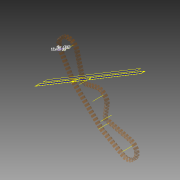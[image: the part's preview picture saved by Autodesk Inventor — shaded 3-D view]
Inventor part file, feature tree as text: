
AUTODESK INVENTOR PART (.ipt)
format: ipt  version: 2014 SP1 (Build 180222100, 222)  size: 551,936 bytes
history: native  units: mm (DEFAULTED — no unit token found)
features: other x93, extrude x84, sketch x4, plane x3, pattern_linear x1
ambient origin geometry x8: Origin, YZ Plane, XZ Plane, XY Plane, X Axis, Y Axis, Z Axis, Center Point
bodies: Body1 (feature_tree), Body2 (feature_tree), Body3 (feature_tree), Body4 (feature_tree), Body5 (feature_tree), Body6 (feature_tree), Body7 (feature_tree), Body8 (feature_tree), Body9 (feature_tree), Body10 (feature_tree), Body11 (feature_tree), Body12 (feature_tree), Body13 (feature_tree), Body14 (feature_tree), Body15 (feature_tree), Body16 (feature_tree), Body17 (feature_tree), Body18 (feature_tree), Body19 (feature_tree), Body20 (feature_tree), Body21 (feature_tree), Body22 (feature_tree), Body23 (feature_tree), Body24 (feature_tree), Body25 (feature_tree), Body26 (feature_tree), Body27 (feature_tree), Body28 (feature_tree), Body29 (feature_tree), Body30 (feature_tree), Body31 (feature_tree), Body32 (feature_tree), Body33 (feature_tree), Body34 (feature_tree), Body35 (feature_tree), Body36 (feature_tree), Body37 (feature_tree), Body38 (feature_tree), Body39 (feature_tree), Body40 (feature_tree), Body41 (feature_tree), Body42 (feature_tree), Body43 (feature_tree), Body44 (feature_tree), Body45 (feature_tree), Body46 (feature_tree), Body47 (feature_tree), Body48 (feature_tree), Body49 (feature_tree), Body50 (feature_tree), Body51 (feature_tree), Body52 (feature_tree), Body53 (feature_tree), Body54 (feature_tree), Body55 (feature_tree), Body56 (feature_tree), Body57 (feature_tree), Body58 (feature_tree), Body59 (feature_tree), Body60 (feature_tree), Body61 (feature_tree), Body62 (feature_tree), Body63 (feature_tree), Body64 (feature_tree), Body65 (feature_tree), Body66 (feature_tree), Body67 (feature_tree), Body68 (feature_tree), Body69 (feature_tree), Body70 (feature_tree), Body71 (feature_tree), Body72 (feature_tree), Body73 (feature_tree), Body74 (feature_tree), Body75 (feature_tree), Body76 (feature_tree), Body77 (feature_tree), Body78 (feature_tree), Body79 (feature_tree), Body80 (feature_tree), Body81 (feature_tree), Body82 (feature_tree), Body83 (feature_tree), Body84 (feature_tree)
feature tree (185):
  sketch  "Sketch Path"  dims[d3=2.682204mm d5=6.981317mm d7=0.0mm d8=0.0mm d9=0.0mm d10=0.0mm d11=0.0mm d12=0.0mm d13=0.0mm d14=0.0mm d15=12.7mm d16=0.0mm d23=6.35mm d24=0.0mm d25=830.0mm]
  other  "Cross Section Plane"
  other  "Work Axis1"
  other  "Work Axis2"
  other  "Work Axis3"
  other  "Work Axis4"
  other  "Work Axis5"
  other  "Work Axis6"
  other  "Work Axis7"
  other  "Cross Section"
  plane  "Work Plane2"
  plane  "Work Plane3"
  sketch  "Sketch4"  dims[d1=10.6172mm]
  plane  "Work Plane4"
  pattern_linear  "Rectangular Pattern3"  Spacing1=6.981317mm  [1 undecoded]
  sketch  "Sketch3"  dims[d0=0.0mm]
  other  "Srf1"
  sketch  "Sketch5"  dims[d2=7.9375mm]
  other  "Srf180"
  other  "Srf181"
  other  "Srf182"
  other  "Srf183"
  other  "Srf184"
  other  "Srf185"
  other  "Srf186"
  other  "Srf187"
  other  "Srf188"
  other  "Srf189"
  other  "Srf190"
  other  "Srf191"
  other  "Srf192"
  other  "Srf193"
  other  "Srf194"
  other  "Srf195"
  other  "Srf196"
  other  "Srf197"
  other  "Srf198"
  other  "Srf199"
  other  "Srf200"
  other  "Srf201"
  other  "Srf202"
  other  "Srf203"
  other  "Srf204"
  other  "Srf205"
  other  "Srf206"
  other  "Srf207"
  other  "Srf208"
  other  "Srf209"
  other  "Srf210"
  other  "Srf211"
  other  "Srf212"
  other  "Srf213"
  other  "Srf214"
  other  "Srf215"
  other  "Srf216"
  other  "Srf217"
  other  "Srf218"
  other  "Srf219"
  other  "Srf220"
  other  "Srf221"
  other  "Srf222"
  other  "Srf223"
  other  "Srf224"
  other  "Srf225"
  other  "Srf226"
  other  "Srf227"
  other  "Srf228"
  other  "Srf229"
  other  "Srf230"
  other  "Srf231"
  other  "Srf232"
  other  "Srf233"
  other  "Srf234"
  other  "Srf235"
  other  "Srf236"
  other  "Srf237"
  other  "Srf238"
  other  "Srf239"
  other  "Srf240"
  other  "Srf241"
  other  "Srf242"
  other  "Srf243"
  other  "Srf244"
  other  "Srf245"
  other  "Srf246"
  other  "Srf247"
  other  "Srf248"
  other  "Srf249"
  other  "Srf250"
  other  "Srf251"
  other  "Srf252"
  other  "Srf253"
  other  "Srf254"
  other  "Srf255"
  other  "Srf256"
  other  "Srf257"
  other  "Srf258"
  other  "Srf259"
  other  "Srf260"
  other  "Srf261"
  other  "Srf262"
  extrude  "ExtrusionSrf1"  TaperAngle=0.0deg  [1 undecoded]
  extrude  "ExtrusionSrf180"  TaperAngle=0.0deg  [1 undecoded]
  extrude  "ExtrusionSrf181"  Depth=12.7mm TaperAngle=0.0deg
  extrude  "ExtrusionSrf182"  Depth=6.35mm TaperAngle=0.0deg
  extrude  "ExtrusionSrf183"  Depth=830.0mm
  extrude  "ExtrusionSrf184"  [1 undecoded]
  extrude  "ExtrusionSrf185"  [1 undecoded]
  extrude  "ExtrusionSrf186"  [1 undecoded]
  extrude  "ExtrusionSrf187"  [1 undecoded]
  extrude  "ExtrusionSrf188"  [1 undecoded]
  extrude  "ExtrusionSrf189"  [1 undecoded]
  extrude  "ExtrusionSrf190"  [1 undecoded]
  extrude  "ExtrusionSrf191"  [1 undecoded]
  extrude  "ExtrusionSrf192"  [1 undecoded]
  extrude  "ExtrusionSrf193"  [1 undecoded]
  extrude  "ExtrusionSrf194"  [1 undecoded]
  extrude  "ExtrusionSrf195"  [1 undecoded]
  extrude  "ExtrusionSrf196"  [1 undecoded]
  extrude  "ExtrusionSrf197"  [1 undecoded]
  extrude  "ExtrusionSrf198"  [1 undecoded]
  extrude  "ExtrusionSrf199"  [1 undecoded]
  extrude  "ExtrusionSrf200"  [1 undecoded]
  extrude  "ExtrusionSrf201"  [1 undecoded]
  extrude  "ExtrusionSrf202"  [1 undecoded]
  extrude  "ExtrusionSrf203"  [1 undecoded]
  extrude  "ExtrusionSrf204"  [1 undecoded]
  extrude  "ExtrusionSrf205"  [1 undecoded]
  extrude  "ExtrusionSrf206"  [1 undecoded]
  extrude  "ExtrusionSrf207"  [1 undecoded]
  extrude  "ExtrusionSrf208"  [1 undecoded]
  extrude  "ExtrusionSrf209"  [1 undecoded]
  extrude  "ExtrusionSrf210"  [1 undecoded]
  extrude  "ExtrusionSrf211"  [1 undecoded]
  extrude  "ExtrusionSrf212"  [1 undecoded]
  extrude  "ExtrusionSrf213"  [1 undecoded]
  extrude  "ExtrusionSrf214"  [1 undecoded]
  extrude  "ExtrusionSrf215"  [1 undecoded]
  extrude  "ExtrusionSrf216"  [1 undecoded]
  extrude  "ExtrusionSrf217"  [1 undecoded]
  extrude  "ExtrusionSrf218"  [1 undecoded]
  extrude  "ExtrusionSrf219"  [1 undecoded]
  extrude  "ExtrusionSrf220"  [1 undecoded]
  extrude  "ExtrusionSrf221"  [1 undecoded]
  extrude  "ExtrusionSrf222"  [1 undecoded]
  extrude  "ExtrusionSrf223"  [1 undecoded]
  extrude  "ExtrusionSrf224"  [1 undecoded]
  extrude  "ExtrusionSrf225"  [1 undecoded]
  extrude  "ExtrusionSrf226"  [1 undecoded]
  extrude  "ExtrusionSrf227"  [1 undecoded]
  extrude  "ExtrusionSrf228"  [1 undecoded]
  extrude  "ExtrusionSrf229"  [1 undecoded]
  extrude  "ExtrusionSrf230"  [1 undecoded]
  extrude  "ExtrusionSrf231"  [1 undecoded]
  extrude  "ExtrusionSrf232"  [1 undecoded]
  extrude  "ExtrusionSrf233"  [1 undecoded]
  extrude  "ExtrusionSrf234"  [1 undecoded]
  extrude  "ExtrusionSrf235"  [1 undecoded]
  extrude  "ExtrusionSrf236"  [1 undecoded]
  extrude  "ExtrusionSrf237"  [1 undecoded]
  extrude  "ExtrusionSrf238"  [1 undecoded]
  extrude  "ExtrusionSrf239"  [1 undecoded]
  extrude  "ExtrusionSrf240"  [1 undecoded]
  extrude  "ExtrusionSrf241"  [1 undecoded]
  extrude  "ExtrusionSrf242"  [1 undecoded]
  extrude  "ExtrusionSrf243"  [1 undecoded]
  extrude  "ExtrusionSrf244"  [1 undecoded]
  extrude  "ExtrusionSrf245"  [1 undecoded]
  extrude  "ExtrusionSrf246"  [1 undecoded]
  extrude  "ExtrusionSrf247"  [1 undecoded]
  extrude  "ExtrusionSrf248"  [1 undecoded]
  extrude  "ExtrusionSrf249"  [1 undecoded]
  extrude  "ExtrusionSrf250"  [1 undecoded]
  extrude  "ExtrusionSrf251"  [1 undecoded]
  extrude  "ExtrusionSrf252"  [1 undecoded]
  extrude  "ExtrusionSrf253"  [1 undecoded]
  extrude  "ExtrusionSrf254"  [1 undecoded]
  extrude  "ExtrusionSrf255"  [1 undecoded]
  extrude  "ExtrusionSrf256"  [1 undecoded]
  extrude  "ExtrusionSrf257"  [1 undecoded]
  extrude  "ExtrusionSrf258"  [1 undecoded]
  extrude  "ExtrusionSrf259"  [1 undecoded]
  extrude  "ExtrusionSrf260"  [1 undecoded]
  extrude  "ExtrusionSrf261"  [1 undecoded]
  extrude  "ExtrusionSrf262"  [1 undecoded]
note: 82 required parameter values undecoded (feature->parameter linkage not recoverable at this tier; creation-order binding heuristic only, values carry confidence <= 0.55)
